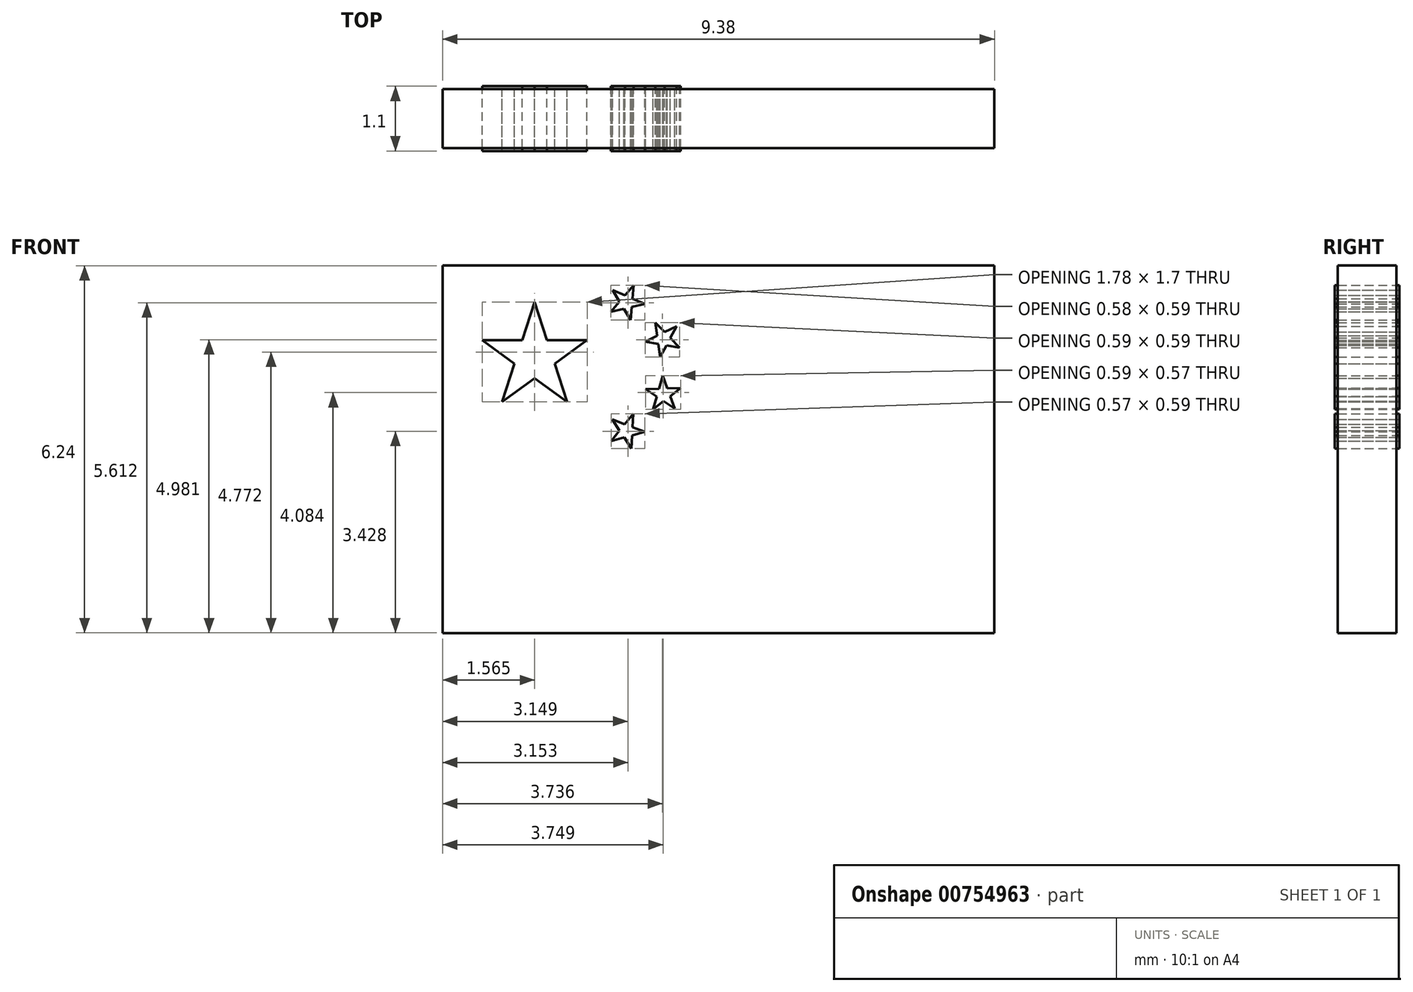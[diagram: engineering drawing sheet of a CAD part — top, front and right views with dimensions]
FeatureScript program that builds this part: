
annotation { "Feature Type Name" : "Feature", "Feature Type Description" : "" }
export const myFeature = defineFeature(function(context is Context, id is Id, definition is map)
    precondition{}
    {
        {
            var Q0;
            Q0=qCreatedBy(makeId("Front.planeOp"),FACE);
            var sketch = newSketch(context, id + "F0", { "sketchPlane" : qUnion([Q0])});
            skLineSegment(sketch, "E0", {"start": v(-4.69, -3.12) * mm, "end": v(4.69, -3.12) * mm});
            skLineSegment(sketch, "E1", {"start": v(4.69, -3.12) * mm, "end": v(4.69, 3.12) * mm});
            skLineSegment(sketch, "E2", {"start": v(4.69, 3.12) * mm, "end": v(-4.69, 3.12) * mm});
            skLineSegment(sketch, "E3", {"start": v(-4.69, 3.12) * mm, "end": v(-4.69, -3.12) * mm});
            skLineSegment(sketch, "E4", {"start": v(-3.12, 2.5) * mm, "end": v(-2.57, 0.8) * mm});
            skLineSegment(sketch, "E5", {"start": v(-2.57, 0.8) * mm, "end": v(-4.02, 1.85) * mm});
            skLineSegment(sketch, "E6", {"start": v(-4.02, 1.85) * mm, "end": v(-2.23, 1.85) * mm});
            skLineSegment(sketch, "E7", {"start": v(-2.23, 1.85) * mm, "end": v(-3.68, 0.8) * mm});
            skLineSegment(sketch, "E8", {"start": v(-3.68, 0.8) * mm, "end": v(-3.13, 2.5) * mm});
            skLineSegment(sketch, "E9", {"start": v(-1.44, 2.79) * mm, "end": v(-1.5, 2.2) * mm});
            skLineSegment(sketch, "E10", {"start": v(-1.5, 2.2) * mm, "end": v(-1.8, 2.7) * mm});
            skLineSegment(sketch, "E11", {"start": v(-1.8, 2.7) * mm, "end": v(-1.25, 2.47) * mm});
            skLineSegment(sketch, "E12", {"start": v(-1.25, 2.47) * mm, "end": v(-1.83, 2.34) * mm});
            skLineSegment(sketch, "E13", {"start": v(-1.83, 2.34) * mm, "end": v(-1.44, 2.79) * mm});
            skLineSegment(sketch, "E14", {"start": v(-0.71, 2.1) * mm, "end": v(-1, 1.57) * mm});
            skLineSegment(sketch, "E15", {"start": v(-1, 1.57) * mm, "end": v(-1.08, 2.16) * mm});
            skLineSegment(sketch, "E16", {"start": v(-1.08, 2.16) * mm, "end": v(-0.66, 1.73) * mm});
            skLineSegment(sketch, "E17", {"start": v(-0.66, 1.73) * mm, "end": v(-1.25, 1.83) * mm});
            skLineSegment(sketch, "E18", {"start": v(-1.25, 1.83) * mm, "end": v(-0.71, 2.1) * mm});
            skLineSegment(sketch, "E19", {"start": v(-0.64, 1.04) * mm, "end": v(-1.11, 0.68) * mm});
            skLineSegment(sketch, "E20", {"start": v(-1.11, 0.68) * mm, "end": v(-0.95, 1.25) * mm});
            skLineSegment(sketch, "E21", {"start": v(-0.95, 1.25) * mm, "end": v(-0.74, 0.7) * mm});
            skLineSegment(sketch, "E22", {"start": v(-0.74, 0.7) * mm, "end": v(-1.24, 1.02) * mm});
            skLineSegment(sketch, "E23", {"start": v(-1.24, 1.02) * mm, "end": v(-0.64, 1.04) * mm});
            skLineSegment(sketch, "E24", {"start": v(-1.45, 0.6) * mm, "end": v(-1.48, 0.01) * mm});
            skLineSegment(sketch, "E25", {"start": v(-1.48, 0.01) * mm, "end": v(-1.8, 0.5) * mm});
            skLineSegment(sketch, "E26", {"start": v(-1.8, 0.5) * mm, "end": v(-1.25, 0.3) * mm});
            skLineSegment(sketch, "E27", {"start": v(-1.25, 0.3) * mm, "end": v(-1.82, 0.14) * mm});
            skLineSegment(sketch, "E28", {"start": v(-1.82, 0.14) * mm, "end": v(-1.45, 0.6) * mm});
            skSolve(sketch);
        }
        {
            var Q0;
            Q0=makeQuery(id+"F0.imprint","IMPRINT",FACE,{"disambiguationData":[TD([[makeQuery(id+"F0.imprint","IMPRINT",EDGE,{"derivedFrom":sQuery(id+"F0.wireOp",EDGE,"E0")}),1.0]])]});
            extrude(context, id + "F1", {"entities" : qUnion([Q0]), "endBound" : BoundingType.SYMMETRIC, "depth" : 1 * mm, "offsetDistance" : 25 * mm});
        }
        {
            var Q0;
            {var subQ1=sQuery(id+"F0.wireOp",EDGE,"E4");var subQ5=sQuery(id+"F0.wireOp",EDGE,"E6");var subQ6=makeQuery(id+"F0.imprint","INTERSECT",VERTEX,{"derivedFrom":[subQ1,subQ5]});Q0=makeQuery(id+"F0.imprint","IMPRINT",FACE,{"disambiguationData":[TD([[makeQuery(id+"F0.imprint","IMPRINT",EDGE,{"disambiguationData":[TD([[subQ6,-1.0]])],"derivedFrom":subQ1}),-1.0]])]});}
            var Q1;
            {var subQ0=sQuery(id+"F0.wireOp",EDGE,"E8");var subQ1=sQuery(id+"F0.wireOp",EDGE,"E4");var subQ2=makeQuery(id+"F0.imprint","INTERSECT",VERTEX,{"derivedFrom":[subQ1,subQ0]});Q1=makeQuery(id+"F0.imprint","IMPRINT",FACE,{"disambiguationData":[TD([[makeQuery(id+"F0.imprint","IMPRINT",EDGE,{"disambiguationData":[TD([[subQ2,-1.0]])],"derivedFrom":subQ1}),-1.0]])]});}
            var Q2;
            {var subQ0=sQuery(id+"F0.wireOp",EDGE,"E6");var subQ1=sQuery(id+"F0.wireOp",EDGE,"E4");var subQ2=makeQuery(id+"F0.imprint","INTERSECT",VERTEX,{"derivedFrom":[subQ1,subQ0]});Q2=makeQuery(id+"F0.imprint","IMPRINT",FACE,{"disambiguationData":[TD([[makeQuery(id+"F0.imprint","IMPRINT",EDGE,{"disambiguationData":[TD([[subQ2,-1.0]])],"derivedFrom":subQ1}),1.0]])]});}
            var Q3;
            {var subQ0=sQuery(id+"F0.wireOp",EDGE,"E6");var subQ1=sQuery(id+"F0.wireOp",EDGE,"E5");var subQ2=makeQuery(id+"F0.imprint","INTERSECT",VERTEX,{"derivedFrom":[subQ1,subQ0]});Q3=makeQuery(id+"F0.imprint","IMPRINT",FACE,{"disambiguationData":[TD([[makeQuery(id+"F0.imprint","IMPRINT",EDGE,{"disambiguationData":[TD([[subQ2,1.0]])],"derivedFrom":subQ1}),-1.0]])]});}
            var Q4;
            {var subQ0=sQuery(id+"F0.wireOp",EDGE,"E7");var subQ1=sQuery(id+"F0.wireOp",EDGE,"E5");var subQ2=makeQuery(id+"F0.imprint","INTERSECT",VERTEX,{"derivedFrom":[subQ1,subQ0]});Q4=makeQuery(id+"F0.imprint","IMPRINT",FACE,{"disambiguationData":[TD([[makeQuery(id+"F0.imprint","IMPRINT",EDGE,{"disambiguationData":[TD([[subQ2,-1.0]])],"derivedFrom":subQ1}),1.0]])]});}
            var Q5;
            {var subQ0=sQuery(id+"F0.wireOp",EDGE,"E5");var subQ1=sQuery(id+"F0.wireOp",EDGE,"E4");var subQ2=makeQuery(id+"F0.imprint","INTERSECT",VERTEX,{"derivedFrom":[subQ1,subQ0]});Q5=makeQuery(id+"F0.imprint","IMPRINT",FACE,{"disambiguationData":[TD([[makeQuery(id+"F0.imprint","IMPRINT",EDGE,{"disambiguationData":[TD([[subQ2,1.0]])],"derivedFrom":subQ1}),-1.0]])]});}
            var Q6;
            {var subQ0=sQuery(id+"F0.wireOp",EDGE,"E26");var subQ1=sQuery(id+"F0.wireOp",EDGE,"E25");var subQ2=makeQuery(id+"F0.imprint","INTERSECT",VERTEX,{"derivedFrom":[subQ1,subQ0]});Q6=makeQuery(id+"F0.imprint","IMPRINT",FACE,{"disambiguationData":[TD([[makeQuery(id+"F0.imprint","IMPRINT",EDGE,{"disambiguationData":[TD([[subQ2,1.0]])],"derivedFrom":subQ1}),-1.0]])]});}
            var Q7;
            {var subQ0=sQuery(id+"F0.wireOp",EDGE,"E28");var subQ1=sQuery(id+"F0.wireOp",EDGE,"E24");var subQ2=makeQuery(id+"F0.imprint","INTERSECT",VERTEX,{"derivedFrom":[subQ1,subQ0]});Q7=makeQuery(id+"F0.imprint","IMPRINT",FACE,{"disambiguationData":[TD([[makeQuery(id+"F0.imprint","IMPRINT",EDGE,{"disambiguationData":[TD([[subQ2,-1.0]])],"derivedFrom":subQ1}),-1.0]])]});}
            var Q8;
            {var subQ0=sQuery(id+"F0.wireOp",EDGE,"E26");var subQ1=sQuery(id+"F0.wireOp",EDGE,"E24");var subQ2=makeQuery(id+"F0.imprint","INTERSECT",VERTEX,{"derivedFrom":[subQ1,subQ0]});Q8=makeQuery(id+"F0.imprint","IMPRINT",FACE,{"disambiguationData":[TD([[makeQuery(id+"F0.imprint","IMPRINT",EDGE,{"disambiguationData":[TD([[subQ2,-1.0]])],"derivedFrom":subQ1}),1.0]])]});}
            var Q9;
            {var subQ0=sQuery(id+"F0.wireOp",EDGE,"E25");var subQ1=sQuery(id+"F0.wireOp",EDGE,"E24");var subQ2=makeQuery(id+"F0.imprint","INTERSECT",VERTEX,{"derivedFrom":[subQ1,subQ0]});Q9=makeQuery(id+"F0.imprint","IMPRINT",FACE,{"disambiguationData":[TD([[makeQuery(id+"F0.imprint","IMPRINT",EDGE,{"disambiguationData":[TD([[subQ2,1.0]])],"derivedFrom":subQ1}),-1.0]])]});}
            var Q10;
            {var subQ1=sQuery(id+"F0.wireOp",EDGE,"E24");var subQ5=sQuery(id+"F0.wireOp",EDGE,"E26");var subQ6=makeQuery(id+"F0.imprint","INTERSECT",VERTEX,{"derivedFrom":[subQ1,subQ5]});Q10=makeQuery(id+"F0.imprint","IMPRINT",FACE,{"disambiguationData":[TD([[makeQuery(id+"F0.imprint","IMPRINT",EDGE,{"disambiguationData":[TD([[subQ6,-1.0]])],"derivedFrom":subQ1}),-1.0]])]});}
            var Q11;
            {var subQ0=sQuery(id+"F0.wireOp",EDGE,"E27");var subQ1=sQuery(id+"F0.wireOp",EDGE,"E25");var subQ2=makeQuery(id+"F0.imprint","INTERSECT",VERTEX,{"derivedFrom":[subQ1,subQ0]});Q11=makeQuery(id+"F0.imprint","IMPRINT",FACE,{"disambiguationData":[TD([[makeQuery(id+"F0.imprint","IMPRINT",EDGE,{"disambiguationData":[TD([[subQ2,-1.0]])],"derivedFrom":subQ1}),1.0]])]});}
            var Q12;
            {var subQ1=sQuery(id+"F0.wireOp",EDGE,"E19");var subQ5=sQuery(id+"F0.wireOp",EDGE,"E21");var subQ6=makeQuery(id+"F0.imprint","INTERSECT",VERTEX,{"derivedFrom":[subQ1,subQ5]});Q12=makeQuery(id+"F0.imprint","IMPRINT",FACE,{"disambiguationData":[TD([[makeQuery(id+"F0.imprint","IMPRINT",EDGE,{"disambiguationData":[TD([[subQ6,-1.0]])],"derivedFrom":subQ1}),-1.0]])]});}
            var Q13;
            {var subQ0=sQuery(id+"F0.wireOp",EDGE,"E21");var subQ1=sQuery(id+"F0.wireOp",EDGE,"E19");var subQ2=makeQuery(id+"F0.imprint","INTERSECT",VERTEX,{"derivedFrom":[subQ1,subQ0]});Q13=makeQuery(id+"F0.imprint","IMPRINT",FACE,{"disambiguationData":[TD([[makeQuery(id+"F0.imprint","IMPRINT",EDGE,{"disambiguationData":[TD([[subQ2,-1.0]])],"derivedFrom":subQ1}),1.0]])]});}
            var Q14;
            {var subQ0=sQuery(id+"F0.wireOp",EDGE,"E20");var subQ1=sQuery(id+"F0.wireOp",EDGE,"E19");var subQ2=makeQuery(id+"F0.imprint","INTERSECT",VERTEX,{"derivedFrom":[subQ1,subQ0]});Q14=makeQuery(id+"F0.imprint","IMPRINT",FACE,{"disambiguationData":[TD([[makeQuery(id+"F0.imprint","IMPRINT",EDGE,{"disambiguationData":[TD([[subQ2,1.0]])],"derivedFrom":subQ1}),-1.0]])]});}
            var Q15;
            {var subQ0=sQuery(id+"F0.wireOp",EDGE,"E21");var subQ1=sQuery(id+"F0.wireOp",EDGE,"E20");var subQ2=makeQuery(id+"F0.imprint","INTERSECT",VERTEX,{"derivedFrom":[subQ1,subQ0]});Q15=makeQuery(id+"F0.imprint","IMPRINT",FACE,{"disambiguationData":[TD([[makeQuery(id+"F0.imprint","IMPRINT",EDGE,{"disambiguationData":[TD([[subQ2,1.0]])],"derivedFrom":subQ1}),-1.0]])]});}
            var Q16;
            {var subQ0=sQuery(id+"F0.wireOp",EDGE,"E22");var subQ1=sQuery(id+"F0.wireOp",EDGE,"E20");var subQ2=makeQuery(id+"F0.imprint","INTERSECT",VERTEX,{"derivedFrom":[subQ1,subQ0]});Q16=makeQuery(id+"F0.imprint","IMPRINT",FACE,{"disambiguationData":[TD([[makeQuery(id+"F0.imprint","IMPRINT",EDGE,{"disambiguationData":[TD([[subQ2,-1.0]])],"derivedFrom":subQ1}),1.0]])]});}
            var Q17;
            {var subQ0=sQuery(id+"F0.wireOp",EDGE,"E23");var subQ1=sQuery(id+"F0.wireOp",EDGE,"E19");var subQ2=makeQuery(id+"F0.imprint","INTERSECT",VERTEX,{"derivedFrom":[subQ1,subQ0]});Q17=makeQuery(id+"F0.imprint","IMPRINT",FACE,{"disambiguationData":[TD([[makeQuery(id+"F0.imprint","IMPRINT",EDGE,{"disambiguationData":[TD([[subQ2,-1.0]])],"derivedFrom":subQ1}),-1.0]])]});}
            var Q18;
            {var subQ0=sQuery(id+"F0.wireOp",EDGE,"E16");var subQ1=sQuery(id+"F0.wireOp",EDGE,"E15");var subQ2=makeQuery(id+"F0.imprint","INTERSECT",VERTEX,{"derivedFrom":[subQ1,subQ0]});Q18=makeQuery(id+"F0.imprint","IMPRINT",FACE,{"disambiguationData":[TD([[makeQuery(id+"F0.imprint","IMPRINT",EDGE,{"disambiguationData":[TD([[subQ2,1.0]])],"derivedFrom":subQ1}),-1.0]])]});}
            var Q19;
            {var subQ0=sQuery(id+"F0.wireOp",EDGE,"E18");var subQ1=sQuery(id+"F0.wireOp",EDGE,"E14");var subQ2=makeQuery(id+"F0.imprint","INTERSECT",VERTEX,{"derivedFrom":[subQ1,subQ0]});Q19=makeQuery(id+"F0.imprint","IMPRINT",FACE,{"disambiguationData":[TD([[makeQuery(id+"F0.imprint","IMPRINT",EDGE,{"disambiguationData":[TD([[subQ2,-1.0]])],"derivedFrom":subQ1}),-1.0]])]});}
            var Q20;
            {var subQ1=sQuery(id+"F0.wireOp",EDGE,"E14");var subQ5=sQuery(id+"F0.wireOp",EDGE,"E16");var subQ6=makeQuery(id+"F0.imprint","INTERSECT",VERTEX,{"derivedFrom":[subQ1,subQ5]});Q20=makeQuery(id+"F0.imprint","IMPRINT",FACE,{"disambiguationData":[TD([[makeQuery(id+"F0.imprint","IMPRINT",EDGE,{"disambiguationData":[TD([[subQ6,-1.0]])],"derivedFrom":subQ1}),-1.0]])]});}
            var Q21;
            {var subQ0=sQuery(id+"F0.wireOp",EDGE,"E16");var subQ1=sQuery(id+"F0.wireOp",EDGE,"E14");var subQ2=makeQuery(id+"F0.imprint","INTERSECT",VERTEX,{"derivedFrom":[subQ1,subQ0]});Q21=makeQuery(id+"F0.imprint","IMPRINT",FACE,{"disambiguationData":[TD([[makeQuery(id+"F0.imprint","IMPRINT",EDGE,{"disambiguationData":[TD([[subQ2,-1.0]])],"derivedFrom":subQ1}),1.0]])]});}
            var Q22;
            {var subQ0=sQuery(id+"F0.wireOp",EDGE,"E15");var subQ1=sQuery(id+"F0.wireOp",EDGE,"E14");var subQ2=makeQuery(id+"F0.imprint","INTERSECT",VERTEX,{"derivedFrom":[subQ1,subQ0]});Q22=makeQuery(id+"F0.imprint","IMPRINT",FACE,{"disambiguationData":[TD([[makeQuery(id+"F0.imprint","IMPRINT",EDGE,{"disambiguationData":[TD([[subQ2,1.0]])],"derivedFrom":subQ1}),-1.0]])]});}
            var Q23;
            {var subQ0=sQuery(id+"F0.wireOp",EDGE,"E17");var subQ1=sQuery(id+"F0.wireOp",EDGE,"E15");var subQ2=makeQuery(id+"F0.imprint","INTERSECT",VERTEX,{"derivedFrom":[subQ1,subQ0]});Q23=makeQuery(id+"F0.imprint","IMPRINT",FACE,{"disambiguationData":[TD([[makeQuery(id+"F0.imprint","IMPRINT",EDGE,{"disambiguationData":[TD([[subQ2,-1.0]])],"derivedFrom":subQ1}),1.0]])]});}
            var Q24;
            {var subQ0=sQuery(id+"F0.wireOp",EDGE,"E13");var subQ1=sQuery(id+"F0.wireOp",EDGE,"E9");var subQ2=makeQuery(id+"F0.imprint","INTERSECT",VERTEX,{"derivedFrom":[subQ1,subQ0]});Q24=makeQuery(id+"F0.imprint","IMPRINT",FACE,{"disambiguationData":[TD([[makeQuery(id+"F0.imprint","IMPRINT",EDGE,{"disambiguationData":[TD([[subQ2,-1.0]])],"derivedFrom":subQ1}),-1.0]])]});}
            var Q25;
            {var subQ1=sQuery(id+"F0.wireOp",EDGE,"E9");var subQ5=sQuery(id+"F0.wireOp",EDGE,"E11");var subQ6=makeQuery(id+"F0.imprint","INTERSECT",VERTEX,{"derivedFrom":[subQ1,subQ5]});Q25=makeQuery(id+"F0.imprint","IMPRINT",FACE,{"disambiguationData":[TD([[makeQuery(id+"F0.imprint","IMPRINT",EDGE,{"disambiguationData":[TD([[subQ6,-1.0]])],"derivedFrom":subQ1}),-1.0]])]});}
            var Q26;
            {var subQ0=sQuery(id+"F0.wireOp",EDGE,"E11");var subQ1=sQuery(id+"F0.wireOp",EDGE,"E10");var subQ2=makeQuery(id+"F0.imprint","INTERSECT",VERTEX,{"derivedFrom":[subQ1,subQ0]});Q26=makeQuery(id+"F0.imprint","IMPRINT",FACE,{"disambiguationData":[TD([[makeQuery(id+"F0.imprint","IMPRINT",EDGE,{"disambiguationData":[TD([[subQ2,1.0]])],"derivedFrom":subQ1}),-1.0]])]});}
            var Q27;
            {var subQ0=sQuery(id+"F0.wireOp",EDGE,"E12");var subQ1=sQuery(id+"F0.wireOp",EDGE,"E10");var subQ2=makeQuery(id+"F0.imprint","INTERSECT",VERTEX,{"derivedFrom":[subQ1,subQ0]});Q27=makeQuery(id+"F0.imprint","IMPRINT",FACE,{"disambiguationData":[TD([[makeQuery(id+"F0.imprint","IMPRINT",EDGE,{"disambiguationData":[TD([[subQ2,-1.0]])],"derivedFrom":subQ1}),1.0]])]});}
            var Q28;
            {var subQ0=sQuery(id+"F0.wireOp",EDGE,"E10");var subQ1=sQuery(id+"F0.wireOp",EDGE,"E9");var subQ2=makeQuery(id+"F0.imprint","INTERSECT",VERTEX,{"derivedFrom":[subQ1,subQ0]});Q28=makeQuery(id+"F0.imprint","IMPRINT",FACE,{"disambiguationData":[TD([[makeQuery(id+"F0.imprint","IMPRINT",EDGE,{"disambiguationData":[TD([[subQ2,1.0]])],"derivedFrom":subQ1}),-1.0]])]});}
            var Q29;
            {var subQ0=sQuery(id+"F0.wireOp",EDGE,"E11");var subQ1=sQuery(id+"F0.wireOp",EDGE,"E9");var subQ2=makeQuery(id+"F0.imprint","INTERSECT",VERTEX,{"derivedFrom":[subQ1,subQ0]});Q29=makeQuery(id+"F0.imprint","IMPRINT",FACE,{"disambiguationData":[TD([[makeQuery(id+"F0.imprint","IMPRINT",EDGE,{"disambiguationData":[TD([[subQ2,-1.0]])],"derivedFrom":subQ1}),1.0]])]});}
            extrude(context, id + "F2", {"entities" : qUnion([Q0, Q1, Q2, Q3, Q4, Q5, Q6, Q7, Q8, Q9, Q10, Q11, Q12, Q13, Q14, Q15, Q16, Q17, Q18, Q19, Q20, Q21, Q22, Q23, Q24, Q25, Q26, Q27, Q28, Q29]), "endBound" : BoundingType.SYMMETRIC, "depth" : 1.1 * mm, "offsetDistance" : 25 * mm});
        }
    });
